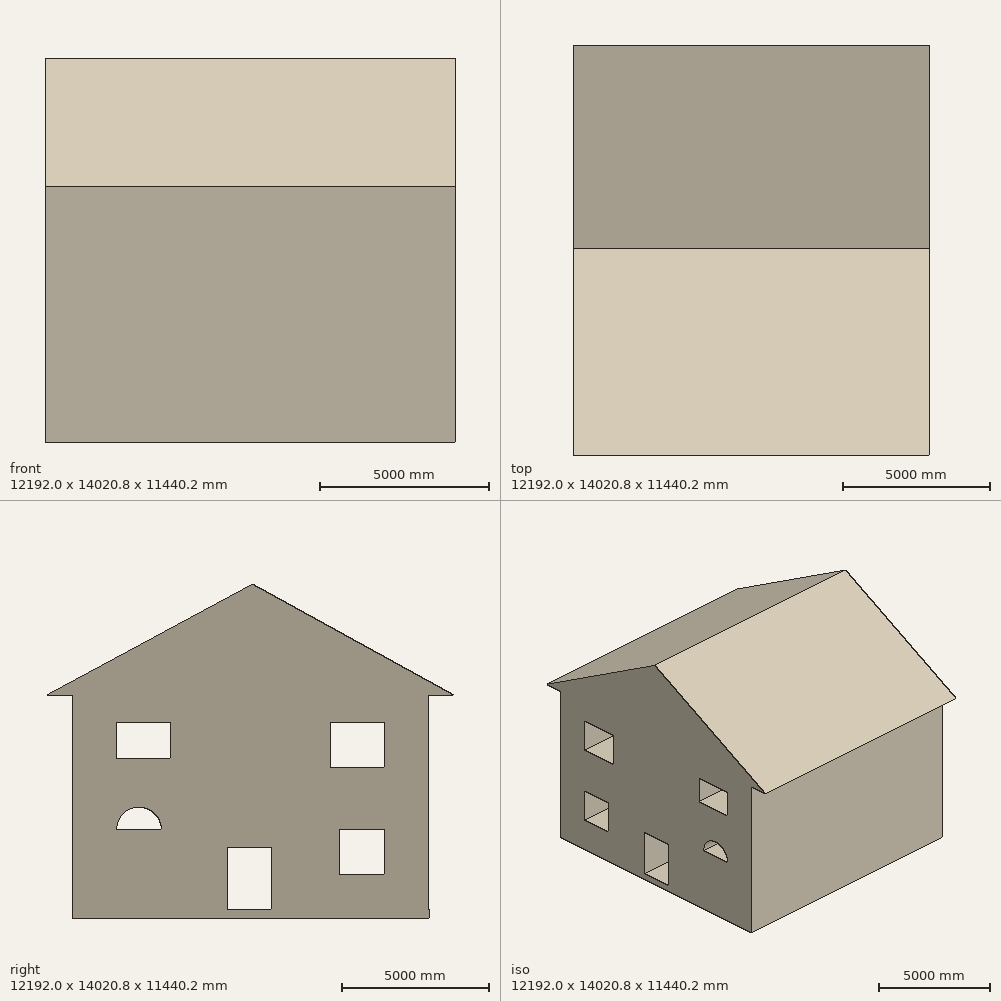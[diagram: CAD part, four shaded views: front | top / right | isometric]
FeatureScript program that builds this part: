
annotation { "Feature Type Name" : "Feature", "Feature Type Description" : "" }
export const myFeature = defineFeature(function(context is Context, id is Id, definition is map)
    precondition{}
    {
        {
            var Q0;
            Q0=qCreatedBy(makeId("Right.planeOp"),FACE);
            var sketch = newSketch(context, id + "F0", { "sketchPlane" : qUnion([Q0])});
            skLineSegment(sketch, "E0", {"start": v(0, 0) * mm, "end": v(-6096, 0) * mm});
            skLineSegment(sketch, "E1", {"start": v(0, 0) * mm, "end": v(6096, 0) * mm});
            skLineSegment(sketch, "E2", {"start": v(-6096, 0) * mm, "end": v(61.84, 3363.24) * mm});
            skLineSegment(sketch, "E3", {"start": v(61.84, 3363.24) * mm, "end": v(6096, 0) * mm});
            skLineSegment(sketch, "E4", {"start": v(-6096, 0) * mm, "end": v(-6096, -7315.2) * mm});
            skLineSegment(sketch, "E5", {"start": v(-6096, -7315.2) * mm, "end": v(6134.13, -7315.2) * mm});
            skLineSegment(sketch, "E6", {"start": v(6096, 0) * mm, "end": v(6096, -7315.2) * mm});
            skLineSegment(sketch, "E7", {"start": v(-6096, -7315.2) * mm, "end": v(-6096, -7620) * mm});
            skLineSegment(sketch, "E8", {"start": v(-6096, -7620) * mm, "end": v(6134.13, -7620) * mm});
            skLineSegment(sketch, "E9", {"start": v(6134.13, -7315.2) * mm, "end": v(6134.13, -7620) * mm});
            skLineSegment(sketch, "E10", {"start": v(0, -7315.2) * mm, "end": v(-792.96, -7315.2) * mm});
            skLineSegment(sketch, "E11", {"start": v(-792.96, -7315.2) * mm, "end": v(-792.96, -5181.6) * mm});
            skLineSegment(sketch, "E12", {"start": v(-792.96, -5181.6) * mm, "end": v(731.04, -5181.6) * mm});
            skLineSegment(sketch, "E13", {"start": v(731.04, -5181.6) * mm, "end": v(731.04, -7315.2) * mm});
            skLineSegment(sketch, "E14", {"start": v(61.84, 3363.24) * mm, "end": v(77.6, 3820.17) * mm});
            skLineSegment(sketch, "E15", {"start": v(6096, 0) * mm, "end": v(7010.4, 0) * mm});
            skLineSegment(sketch, "E16", {"start": v(-6096, 0) * mm, "end": v(-7010.4, 0) * mm});
            skLineSegment(sketch, "E17", {"start": v(-7010.4, 0) * mm, "end": v(77.6, 3820.17) * mm});
            skLineSegment(sketch, "E18", {"start": v(77.6, 3820.17) * mm, "end": v(7010.4, 0) * mm});
            skLineSegment(sketch, "E19.bottom", {"start": v(-4572, -914.4) * mm, "end": v(-2743.2, -914.4) * mm});
            skLineSegment(sketch, "E19.top", {"start": v(-4572, -2133.6) * mm, "end": v(-2743.2, -2133.6) * mm});
            skLineSegment(sketch, "E19.left", {"start": v(-4572, -914.4) * mm, "end": v(-4572, -2133.6) * mm});
            skLineSegment(sketch, "E19.right", {"start": v(-2743.2, -914.4) * mm, "end": v(-2743.2, -2133.6) * mm});
            skLineSegment(sketch, "E20.bottom", {"start": v(2743.2, -914.4) * mm, "end": v(4572, -914.4) * mm});
            skLineSegment(sketch, "E20.top", {"start": v(2743.2, -2438.4) * mm, "end": v(4572, -2438.4) * mm});
            skLineSegment(sketch, "E20.left", {"start": v(2743.2, -914.4) * mm, "end": v(2743.2, -2438.4) * mm});
            skLineSegment(sketch, "E20.right", {"start": v(4572, -914.4) * mm, "end": v(4572, -2438.4) * mm});
            skLineSegment(sketch, "E21.bottom", {"start": v(-4572, -4572) * mm, "end": v(-3048, -4572) * mm});
            skLineSegment(sketch, "E21.top", {"start": v(-4572, -6096) * mm, "end": v(-3048, -6096) * mm});
            skLineSegment(sketch, "E21.left", {"start": v(-4572, -4572) * mm, "end": v(-4572, -6096) * mm});
            skLineSegment(sketch, "E21.right", {"start": v(-3048, -4572) * mm, "end": v(-3048, -6096) * mm});
            skArc(sketch, "E22", {"start": v(-3048, -4572) * mm, "mid": v(-3810, -3810) * mm, "end": v(-4572, -4572) * mm});
            skLineSegment(sketch, "E23.bottom", {"start": v(3048, -6096) * mm, "end": v(4572, -6096) * mm});
            skLineSegment(sketch, "E23.top", {"start": v(3048, -4572) * mm, "end": v(4572, -4572) * mm});
            skLineSegment(sketch, "E23.left", {"start": v(3048, -6096) * mm, "end": v(3048, -4572) * mm});
            skLineSegment(sketch, "E23.right", {"start": v(4572, -6096) * mm, "end": v(4572, -4572) * mm});
            skSolve(sketch);
        }
        {
            var Q0;
            Q0=makeQuery(id+"F0.imprint","IMPRINT",FACE,{"disambiguationData":[TD([[makeQuery(id+"F0.imprint","IMPRINT",EDGE,{"derivedFrom":sQuery(id+"F0.wireOp",EDGE,"E0")}),-1.0]])]});
            var Q1;
            Q1=makeQuery(id+"F0.imprint","IMPRINT",FACE,{"disambiguationData":[TD([[makeQuery(id+"F0.imprint","IMPRINT",EDGE,{"derivedFrom":sQuery(id+"F0.wireOp",EDGE,"E0")}),1.0]])]});
            var Q2;
            {var subQ0=sQuery(id+"F0.wireOp",EDGE,"E10");Q2=makeQuery(id+"F0.imprint","IMPRINT",FACE,{"disambiguationData":[TD([[makeQuery(id+"F0.imprint","IMPRINT",EDGE,{"derivedFrom":subQ0}),-1.0]])]});}
            var Q3;
            Q3=makeQuery(id+"F0.imprint","IMPRINT",FACE,{"disambiguationData":[TD([[makeQuery(id+"F0.imprint","IMPRINT",EDGE,{"derivedFrom":sQuery(id+"F0.wireOp",EDGE,"E21.bottom")}),-1.0]])]});
            var Q4;
            {var subQ5=sQuery(id+"F0.wireOp",EDGE,"E7");Q4=makeQuery(id+"F0.imprint","IMPRINT",FACE,{"disambiguationData":[TD([[makeQuery(id+"F0.imprint","IMPRINT",EDGE,{"derivedFrom":subQ5}),1.0]])]});}
            var Q5;
            Q5=makeQuery(id+"F0.imprint","IMPRINT",FACE,{"disambiguationData":[TD([[makeQuery(id+"F0.imprint","IMPRINT",EDGE,{"derivedFrom":sQuery(id+"F0.wireOp",EDGE,"E3")}),1.0]])]});
            var Q6;
            Q6=makeQuery(id+"F0.imprint","IMPRINT",FACE,{"disambiguationData":[TD([[makeQuery(id+"F0.imprint","IMPRINT",EDGE,{"derivedFrom":sQuery(id+"F0.wireOp",EDGE,"E2")}),1.0]])]});
            extrude(context, id + "F1", {"entities" : qUnion([Q0, Q1, Q2, Q3, Q4, Q5, Q6]), "depth" : 12192 * mm, "offsetDistance" : 30.48 * mm});
        }
    });
